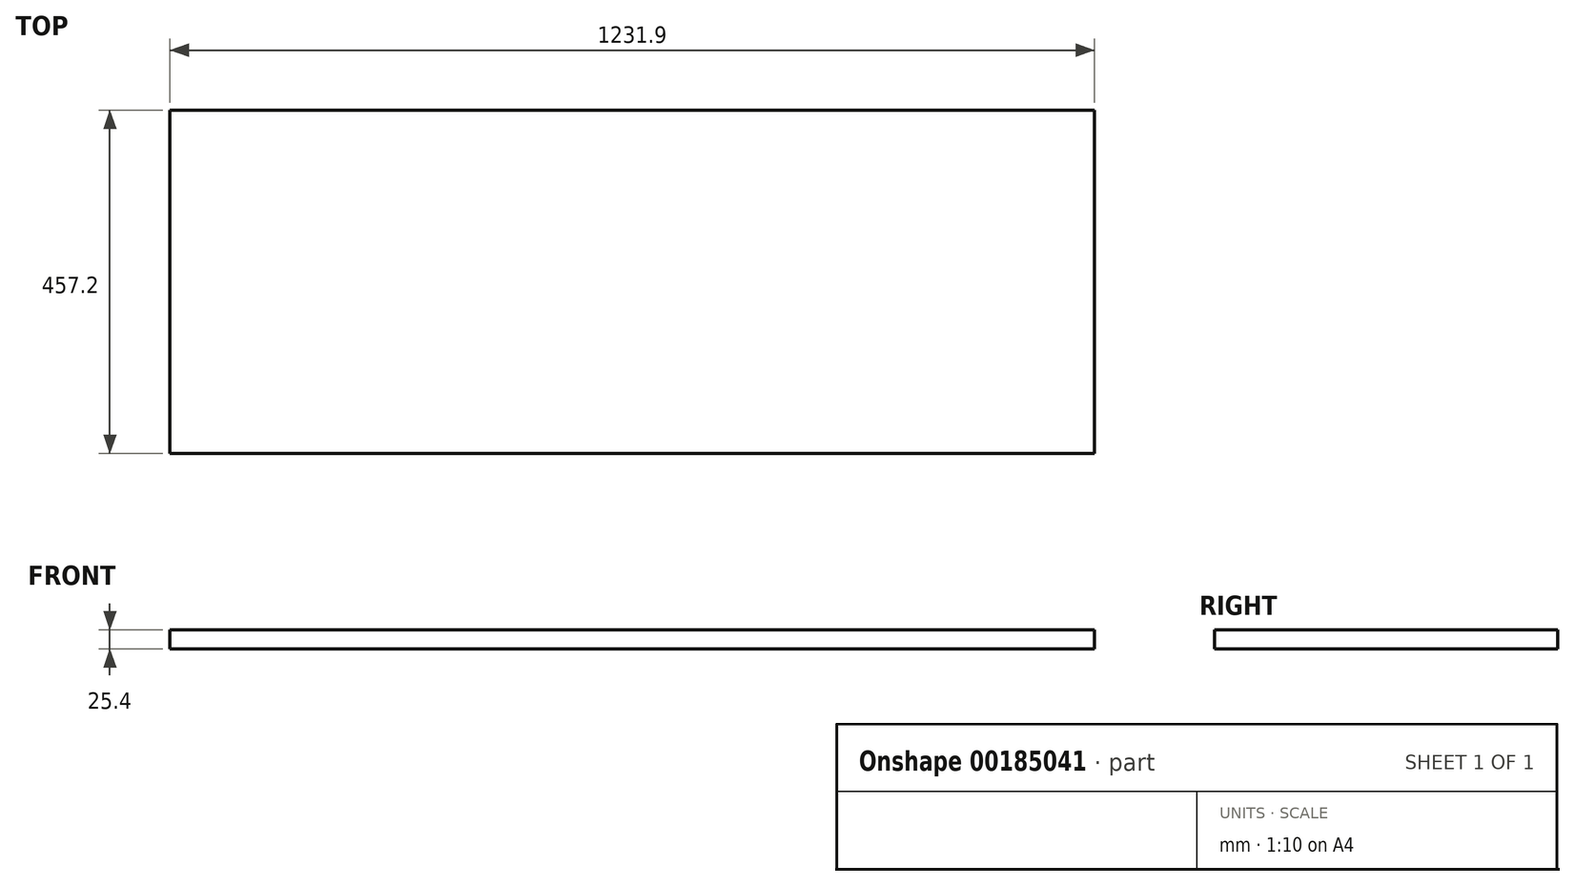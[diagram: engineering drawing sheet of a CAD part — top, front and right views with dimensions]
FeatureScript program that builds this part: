
annotation { "Feature Type Name" : "Feature", "Feature Type Description" : "" }
export const myFeature = defineFeature(function(context is Context, id is Id, definition is map)
    precondition{}
    {
        {
            var Q0;
            Q0=qCreatedBy(makeId("Top.planeOp"),FACE);
            var sketch = newSketch(context, id + "F0", { "sketchPlane" : qUnion([Q0])});
            skLineSegment(sketch, "E0.bottom", {"start": v(615.95, 228.6) * mm, "end": v(-615.95, 228.6) * mm});
            skLineSegment(sketch, "E0.top", {"start": v(615.95, -228.6) * mm, "end": v(-615.95, -228.6) * mm});
            skLineSegment(sketch, "E0.left", {"start": v(615.95, 228.6) * mm, "end": v(615.95, -228.6) * mm});
            skLineSegment(sketch, "E0.right", {"start": v(-615.95, 228.6) * mm, "end": v(-615.95, -228.6) * mm});
            skPoint(sketch, "E0.middle", {"position": v(0, 0) * mm});
            skSolve(sketch);
        }
        {
            var Q0;
            Q0 = qSketchRegion(id + "F0", true);
            extrude(context, id + "F1", {"entities" : qUnion([Q0]), "depth" : 25.4 * mm});
        }
    });
